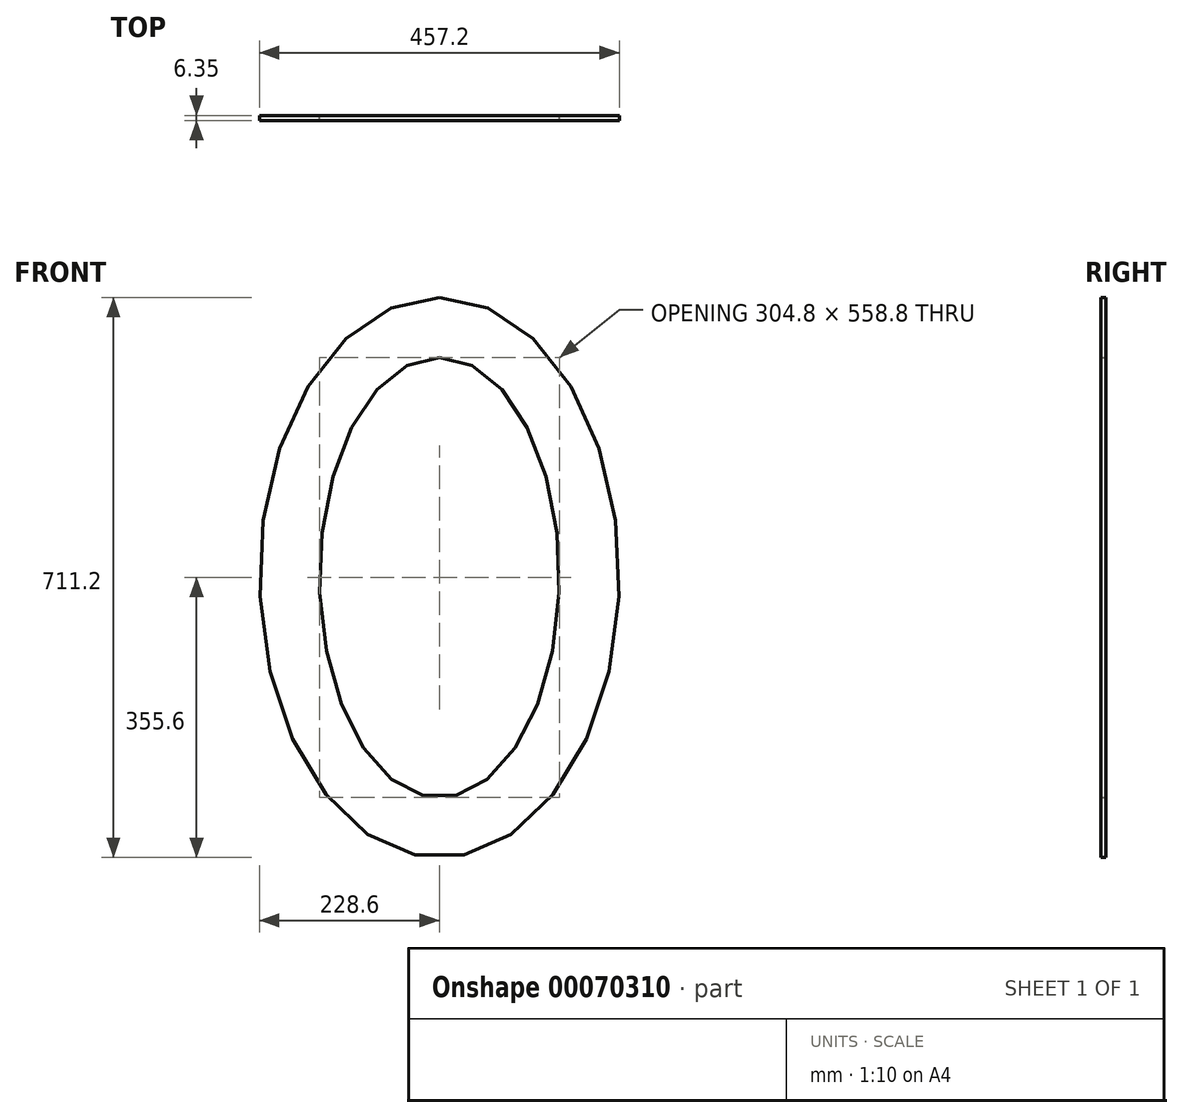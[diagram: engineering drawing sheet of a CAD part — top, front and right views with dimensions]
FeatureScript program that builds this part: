
annotation { "Feature Type Name" : "Feature", "Feature Type Description" : "" }
export const myFeature = defineFeature(function(context is Context, id is Id, definition is map)
    precondition{}
    {
        {
            var Q0;
            Q0=qCreatedBy(makeId("Front.planeOp"),FACE);
            var sketch = newSketch(context, id + "F0", { "sketchPlane" : qUnion([Q0])});
            skEllipse(sketch, "E0", {"center": v(0, 0) * mm, "majorRadius": 355.6 * mm, "minorRadius": 228.6 * mm, "majorAxis": v(0, 1)});
            skEllipse(sketch, "E1", {"center": v(0, 0) * mm, "majorRadius": 279.4 * mm, "minorRadius": 152.4 * mm, "majorAxis": v(0, 1)});
            skSolve(sketch);
        }
        {
            var Q0;
            Q0 = qSketchRegion(id + "F0", true);
            extrude(context, id + "F1", {"entities" : qUnion([Q0]), "depth" : 6.35 * mm});
        }
    });
